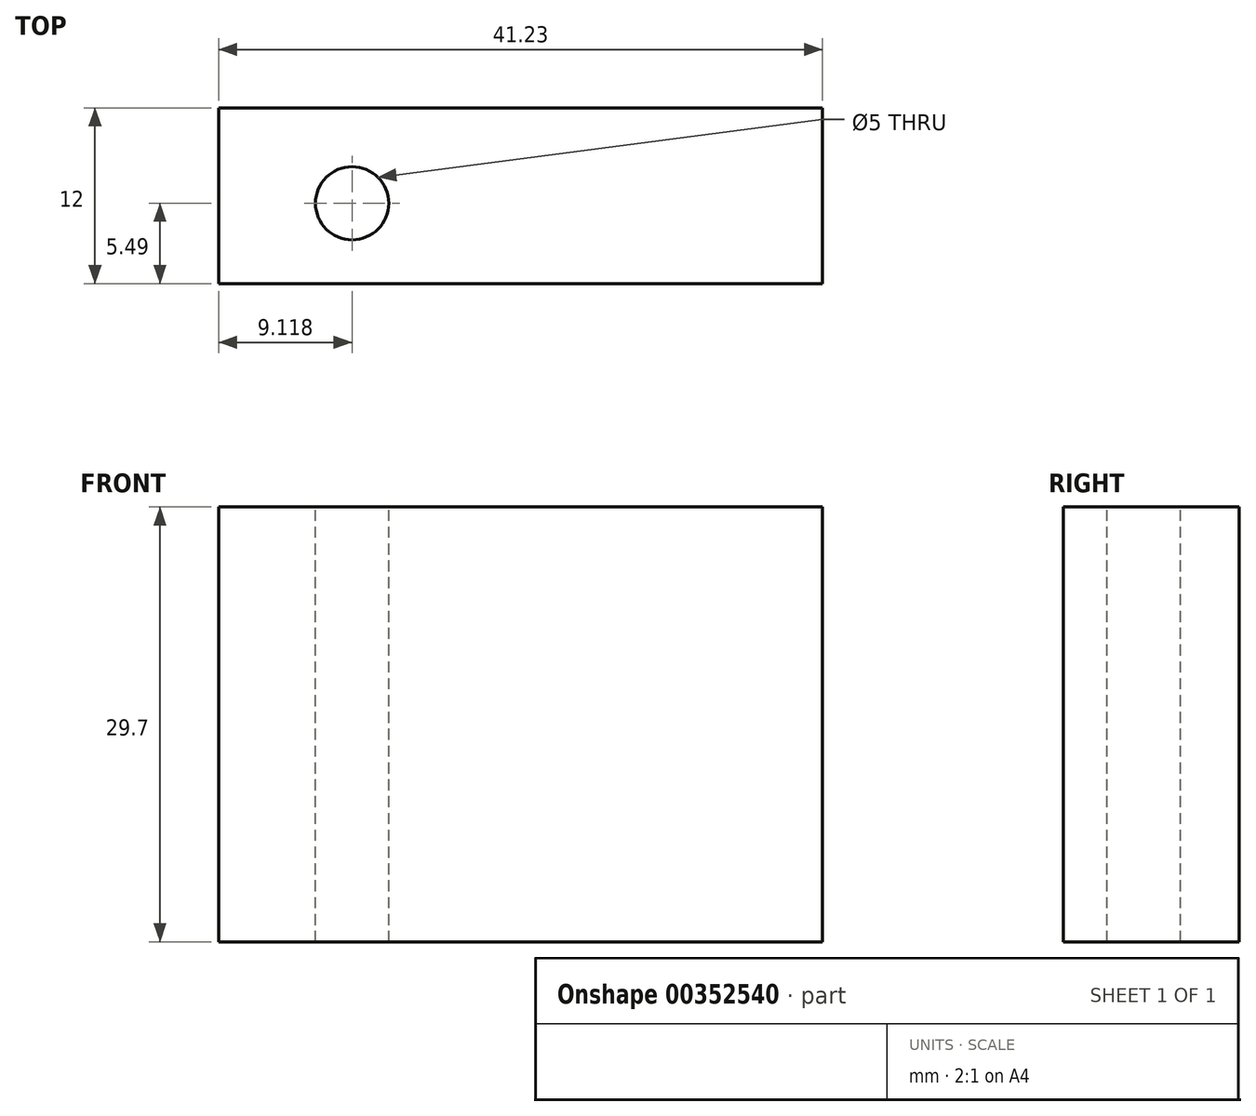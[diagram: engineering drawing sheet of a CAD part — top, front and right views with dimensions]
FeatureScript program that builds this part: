
annotation { "Feature Type Name" : "Feature", "Feature Type Description" : "" }
export const myFeature = defineFeature(function(context is Context, id is Id, definition is map)
    precondition{}
    {
        {
            var Q0;
            Q0=qCreatedBy(makeId("Front.planeOp"),FACE);
            var sketch = newSketch(context, id + "F0", { "sketchPlane" : qUnion([Q0])});
            skLineSegment(sketch, "E0.bottom", {"start": v(-20.36, 14.34) * mm, "end": v(20.87, 14.34) * mm});
            skLineSegment(sketch, "E0.top", {"start": v(-20.36, -15.36) * mm, "end": v(20.87, -15.36) * mm});
            skLineSegment(sketch, "E0.left", {"start": v(-20.36, 14.34) * mm, "end": v(-20.36, -15.36) * mm});
            skLineSegment(sketch, "E0.right", {"start": v(20.87, 14.34) * mm, "end": v(20.87, -15.36) * mm});
            skSolve(sketch);
        }
        {
            var Q0;
            Q0=qCreatedBy(makeId("Top.planeOp"),FACE);
            var sketch = newSketch(context, id + "F1", { "sketchPlane" : qUnion([Q0])});
            skCircle(sketch, "E1", {"center": v(0, 0) * mm, "radius": 5.51 * mm});
            skSolve(sketch);
        }
        {
            var Q0;
            Q0 = qSketchRegion(id + "F0", true);
            extrude(context, id + "F2", {"entities" : qUnion([Q0]), "depth" : 12 * mm});
        }
        {
            var Q0;
            Q0=sQuery(id+"F1.wireOp",EDGE,"E1");
            extrude(context, id + "F3", {"bodyType" : ToolBodyType.SURFACE, "surfaceEntities" : qUnion([Q0]), "depth" : 25 * mm});
        }
        {
            var Q0;
            Q0=makeQuery(id+"F2.opExtrude","SWEPT_FACE",FACE,{"disambiguationData":[OSD([sQuery(id+"F0.wireOp",EDGE,"E0.bottom")])]});
            var sketch = newSketch(context, id + "F4", { "sketchPlane" : qUnion([Q0])});
            skCircle(sketch, "E2", {"center": v(-11.24, -6.5) * mm, "radius": 4.28 * mm});
            skSolve(sketch);
        }
        {
            var Q0;
            Q0=sQuery(id+"F4.wireOp",VERTEX,"E2.center");
            var Q1;
            Q1=makeQuery(id+"F2.opExtrude","SWEPT_BODY",BODY,{"disambiguationData":[OSD([sQuery(id+"F0.wireOp",EDGE,"E0.bottom"),sQuery(id+"F0.wireOp",EDGE,"E0.top"),sQuery(id+"F0.wireOp",EDGE,"E0.left"),sQuery(id+"F0.wireOp",EDGE,"E0.right")])]});
            hole(context, id + "F5", {"style" : HoleStyle.SIMPLE, "endStyle" : HoleEndStyle.THROUGH, "holeDiameter" : 5 * mm, "isTappedThrough" : true, "tappedDepth" : 12 * mm, "tapClearance" : 3, "locations" : qUnion([Q0]), "scope" : qUnion([Q1])});
        }
    });
